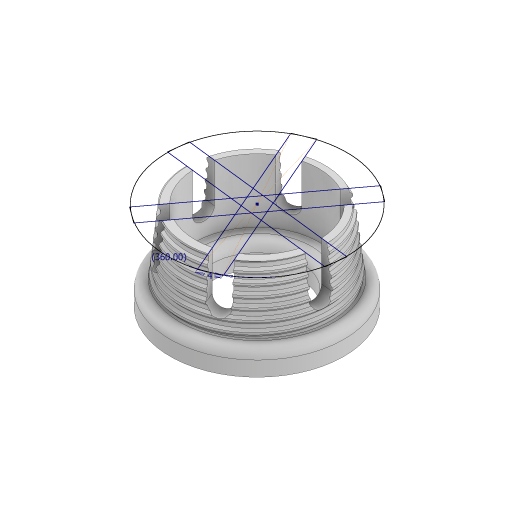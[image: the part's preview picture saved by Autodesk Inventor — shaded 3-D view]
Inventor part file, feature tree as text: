
AUTODESK INVENTOR PART (.ipt)
format: ipt  version: 2023 (Build 270158000, 158)  size: 991,744 bytes
history: native  units: mm
features: sketch x3, extrude x3, helix x2, fillet x2, revolve x1
ambient origin geometry x8: Origin, YZ Plane, XZ Plane, XY Plane, X Axis, Y Axis, Z Axis, Center Point
bodies: Solid1 (feature_tree)
feature tree (11):
  sketch  "Sketch2"  dims[d2=12.5mm d3=1.2mm d4=16.755161mm d5=90.0deg]
  revolve  "Revolution1"  [1 undecoded]
  helix  "Coil1"  [1 undecoded]
  helix  "Coil2"  [1 undecoded]
  sketch  "Sketch3"  dims[d6=12.875mm d7=2.0mm d8=12.875mm]
  extrude  "Extrusion1"  Depth=2.0mm
  extrude  "Extrusion2"  TaperAngle=90.0deg  [1 undecoded]
  extrude  "Extrusion3"  Depth=2.0mm
  fillet  "Fillet1"  [1 undecoded]
  fillet  "Fillet2"  Radius=4.0mm
  sketch  "Sketch4"  dims[d9=10.0mm d10=1.047198mm d11=90.0deg d12=90.0deg d13=0.0mm d14=0.0mm d15=2.0mm d16=2.0mm d17=10.0mm d18=-1.047198mm d19=90.0deg d20=90.0deg d21=0.0mm d22=0.0mm d23=4.0mm d24=30.0mm d26=360.0deg d28=0.0mm d29=0.0mm d30=10.0mm d31=0.0mm d32=5.0mm d33=0.0mm d34=2.0mm d35=2.0mm]
note: 5 required parameter values undecoded (feature->parameter linkage not recoverable at this tier; creation-order binding heuristic only, values carry confidence <= 0.55)